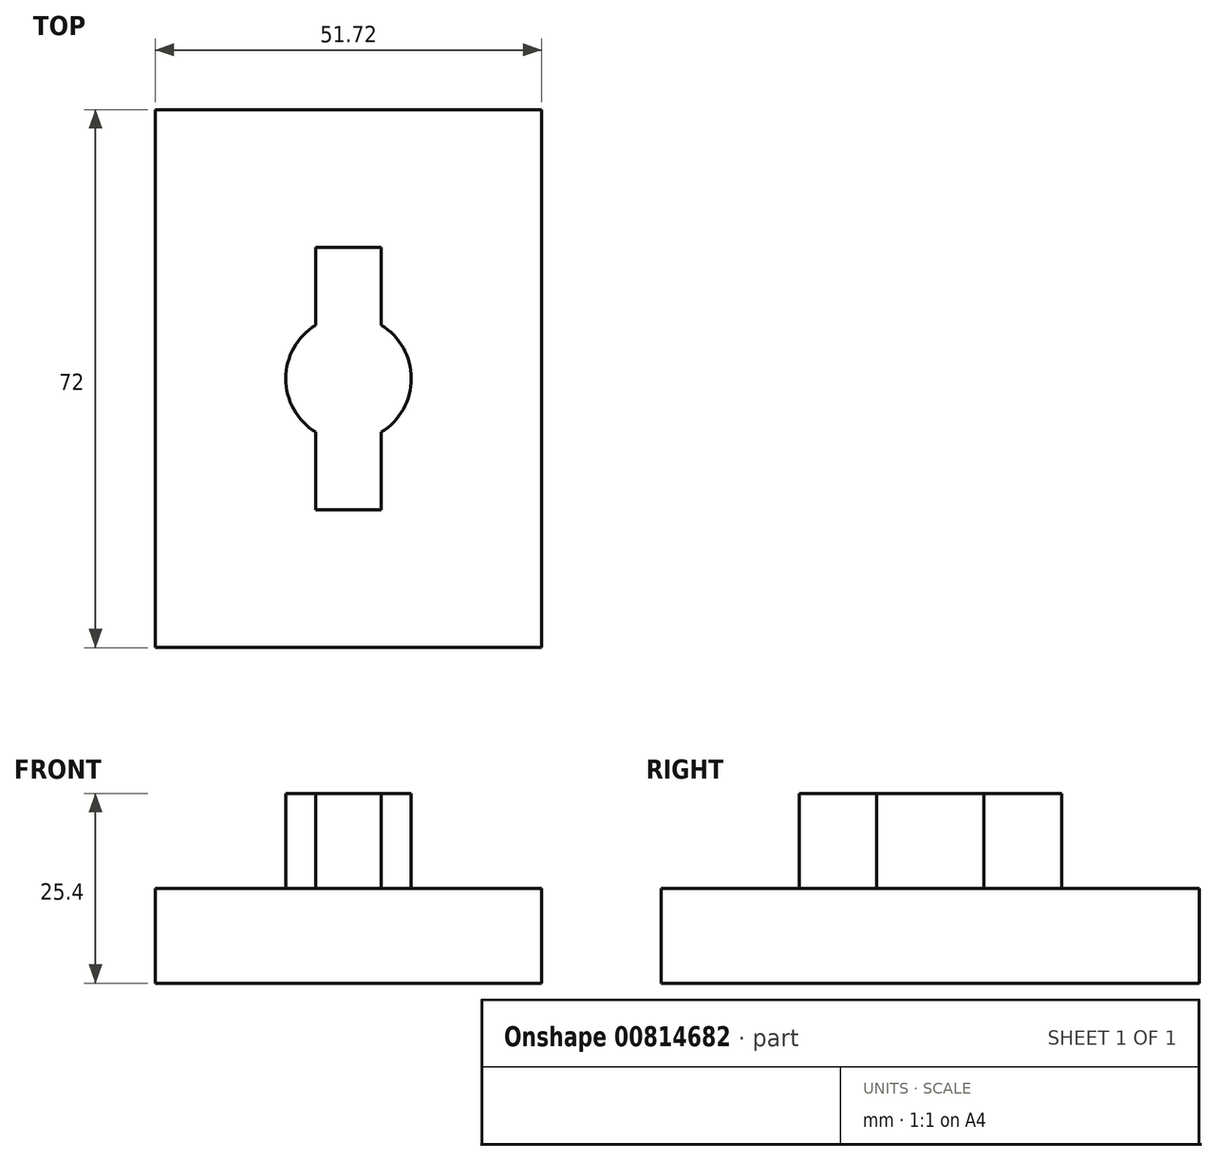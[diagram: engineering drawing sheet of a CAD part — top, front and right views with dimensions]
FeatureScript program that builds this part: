
annotation { "Feature Type Name" : "Feature", "Feature Type Description" : "" }
export const myFeature = defineFeature(function(context is Context, id is Id, definition is map)
    precondition{}
    {
        {
            var Q0;
            Q0=qCreatedBy(makeId("Top.planeOp"),FACE);
            var sketch = newSketch(context, id + "F0", { "sketchPlane" : qUnion([Q0])});
            skLineSegment(sketch, "E0.bottom", {"start": v(-25.86, 36) * mm, "end": v(25.86, 36) * mm});
            skLineSegment(sketch, "E0.top", {"start": v(-25.86, -36) * mm, "end": v(25.86, -36) * mm});
            skLineSegment(sketch, "E0.left", {"start": v(-25.86, 36) * mm, "end": v(-25.86, -36) * mm});
            skLineSegment(sketch, "E0.right", {"start": v(25.86, 36) * mm, "end": v(25.86, -36) * mm});
            skPoint(sketch, "E0.middle", {"position": v(0, 0) * mm});
            skCircle(sketch, "E1", {"center": v(0, 0) * mm, "radius": 8.4 * mm});
            skLineSegment(sketch, "E2.bottom", {"start": v(-4.39, 17.54) * mm, "end": v(4.39, 17.54) * mm});
            skLineSegment(sketch, "E2.top", {"start": v(-4.39, -17.54) * mm, "end": v(4.39, -17.54) * mm});
            skLineSegment(sketch, "E2.left", {"start": v(-4.39, 17.54) * mm, "end": v(-4.39, -17.54) * mm});
            skLineSegment(sketch, "E2.right", {"start": v(4.39, 17.54) * mm, "end": v(4.39, -17.54) * mm});
            skSolve(sketch);
        }
        {
            var Q0;
            {var subQ0=sQuery(id+"F0.wireOp",EDGE,"E2.right");var subQ1=sQuery(id+"F0.wireOp",EDGE,"E1");var subQ2=makeQuery(id+"F0.imprint","INTERSECT",VERTEX,{"disambiguationData":[OD(0.0)],"derivedFrom":[subQ1,subQ0]});Q0=makeQuery(id+"F0.imprint","IMPRINT",FACE,{"disambiguationData":[TD([[makeQuery(id+"F0.imprint","IMPRINT",EDGE,{"disambiguationData":[TD([[subQ2,1.0]])],"derivedFrom":subQ1}),1.0]])]});}
            var Q1;
            {var subQ0=sQuery(id+"F0.wireOp",EDGE,"E2.left");var subQ1=sQuery(id+"F0.wireOp",EDGE,"E1");var subQ2=makeQuery(id+"F0.imprint","INTERSECT",VERTEX,{"disambiguationData":[OD(0.0)],"derivedFrom":[subQ1,subQ0]});Q1=makeQuery(id+"F0.imprint","IMPRINT",FACE,{"disambiguationData":[TD([[makeQuery(id+"F0.imprint","IMPRINT",EDGE,{"disambiguationData":[TD([[subQ2,1.0]])],"derivedFrom":subQ1}),1.0]])]});}
            var Q2;
            {var subQ0=sQuery(id+"F0.wireOp",EDGE,"E2.left");var subQ1=sQuery(id+"F0.wireOp",EDGE,"E1");var subQ2=makeQuery(id+"F0.imprint","INTERSECT",VERTEX,{"disambiguationData":[OD(0.0)],"derivedFrom":[subQ1,subQ0]});Q2=makeQuery(id+"F0.imprint","IMPRINT",FACE,{"disambiguationData":[TD([[makeQuery(id+"F0.imprint","IMPRINT",EDGE,{"disambiguationData":[TD([[subQ2,-1.0]])],"derivedFrom":subQ1}),1.0]])]});}
            var Q3;
            {var subQ5=sQuery(id+"F0.wireOp",EDGE,"E2.top");Q3=makeQuery(id+"F0.imprint","IMPRINT",FACE,{"disambiguationData":[TD([[makeQuery(id+"F0.imprint","IMPRINT",EDGE,{"derivedFrom":subQ5}),1.0]])]});}
            var Q4;
            {var subQ5=sQuery(id+"F0.wireOp",EDGE,"E2.bottom");Q4=makeQuery(id+"F0.imprint","IMPRINT",FACE,{"disambiguationData":[TD([[makeQuery(id+"F0.imprint","IMPRINT",EDGE,{"derivedFrom":subQ5}),-1.0]])]});}
            extrude(context, id + "F1", {"entities" : qUnion([Q0, Q1, Q2, Q3, Q4]), "depth" : 25.4 * mm, "offsetDistance" : 25.4 * mm});
        }
        {
            var Q0;
            Q0 = qSketchRegion(id + "F0", true);
            extrude(context, id + "F2", {"entities" : qUnion([Q0]), "operationType" : NewBodyOperationType.ADD, "depth" : 12.7 * mm, "offsetDistance" : 25.4 * mm});
        }
    });
